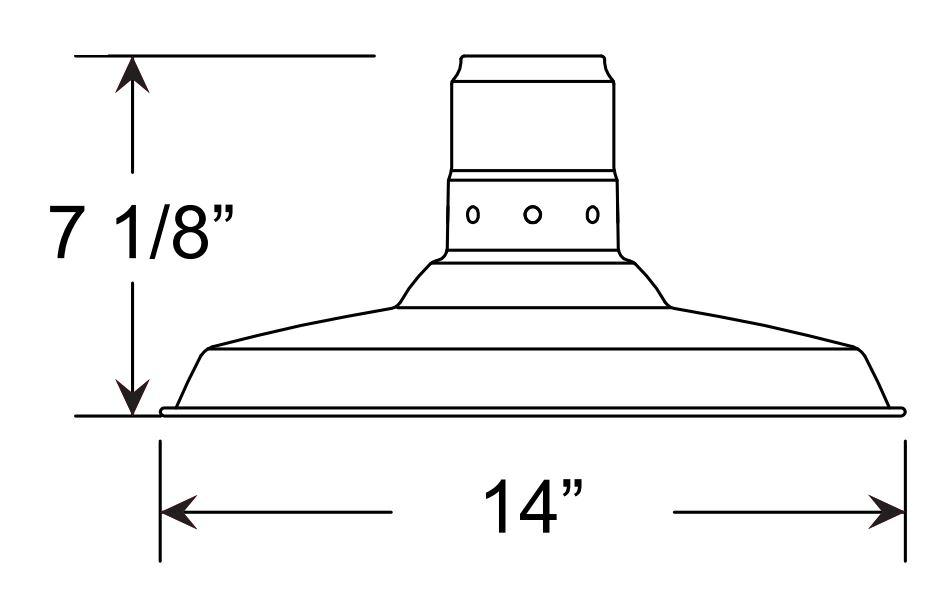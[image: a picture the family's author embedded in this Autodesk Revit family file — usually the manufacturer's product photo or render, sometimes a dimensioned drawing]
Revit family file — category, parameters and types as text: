
# Revit family: OSAB_MB
name_source: partatom
category: Lighting Fixtures
units: mm (PartAtom-declared; Revit-internal decimal feet)

## family parameters
Always vertical = Yes
Cut with Voids When Loaded = No
Light Source = Yes
OmniClass Number = 23.80.70.00
OmniClass Title = Lighting
Part Type = Normal
Room Calculation Point = No
Round Connector Dimension = Use Diameter
Shared = No
Work Plane-Based = No

## types (3) — shared parameters
Apparent Load = 200 VA
Body Colour = Spun aluminium
Body Material = body
Bulb = BULB
CRI = >90
Color Filter = 16777215
Construction Material = Heavy Duty spun aluminum.
Default Elevation = 0' - 0"
Description = 120-277 Voltage
Dimming = 1%
Dimming Lamp Color Temperature Shift = <None>
Efficiency = 65-125 lumens per watt
GLASS = Glass
Inside body material = INSIDE BODY MATERIAL
Lamp = 200W MAX MEDIUM BASE
Life = L70 50,000 hours
Load Classification = Lighting
Manufacturer = ANP Lighting
Photometric Web File = OSAB42M037LDNW40K.IES
Power Factor = 1
Tilt Angle = 90.00°
URL = https://www.anplighting.com
Voltage = 277 V
Warranty = 5 year limited warranty
Wattage Comments = 200W

## per-type parameters (varying)
| type | Fixture Diameter | Fixture Height | OSAB24 | OSAB36 | OSAB42 | Weight |
| OSAB24 | 2' - 0" | 1' - 2" | Yes | No | No | 10.5 lb |
| OSAB36 | 3' - 0" | 1' - 9" | No | Yes | No | 19.0 lb |
| OSAB42 | 3' - 6" | 2' - 0" | No | No | Yes | 22.0 lb |

note: column(s) folded — value = type name in every type: Model

## geometry (parser evidence)
native form markers: Sweep x36
no freeform markers — native parametric forms only
